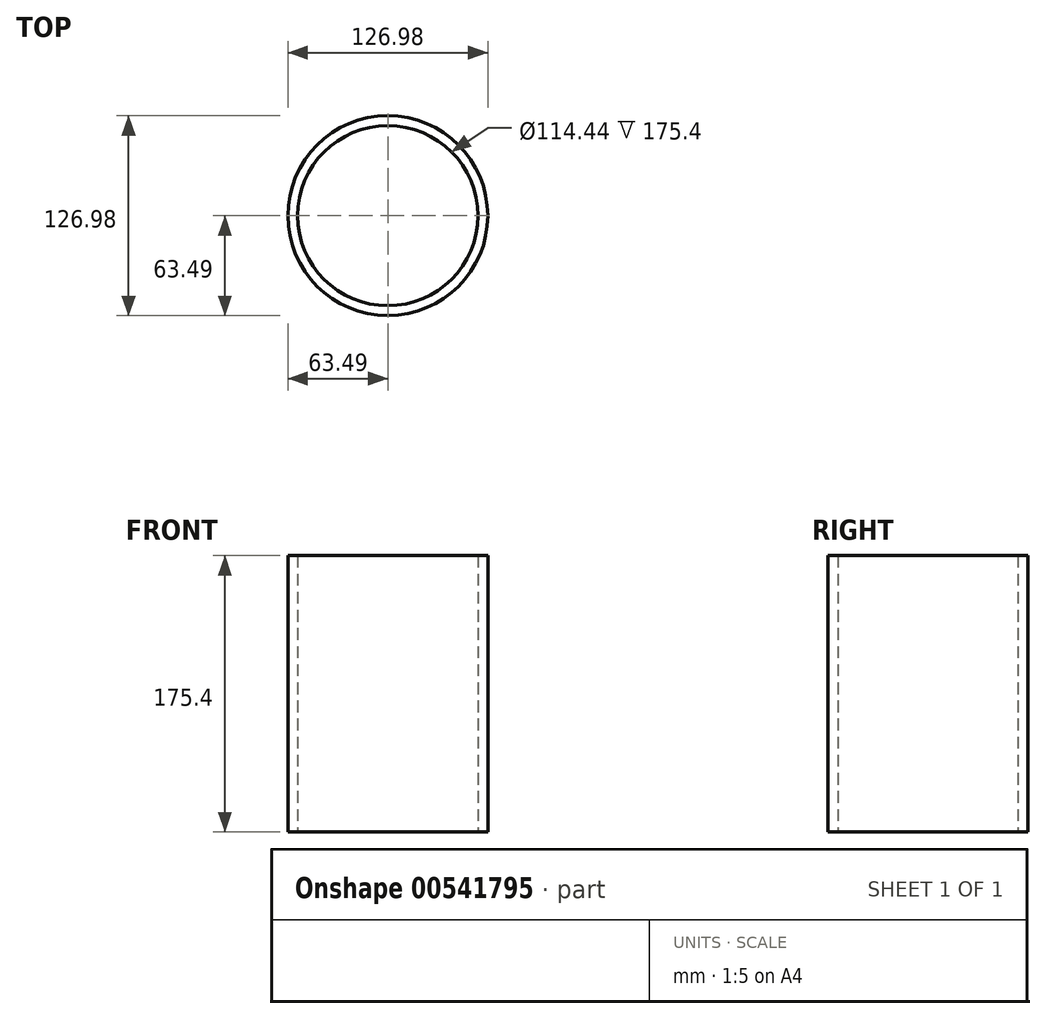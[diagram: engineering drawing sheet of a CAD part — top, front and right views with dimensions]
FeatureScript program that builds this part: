
annotation { "Feature Type Name" : "Feature", "Feature Type Description" : "" }
export const myFeature = defineFeature(function(context is Context, id is Id, definition is map)
    precondition{}
    {
        {
            var Q0;
            Q0=qCreatedBy(makeId("Top.planeOp"),FACE);
            var sketch = newSketch(context, id + "F0", { "sketchPlane" : qUnion([Q0])});
            skCircle(sketch, "E0", {"center": v(0, 0) * mm, "radius": 63.5 * mm});
            skCircle(sketch, "E1", {"center": v(0, 0) * mm, "radius": 57.22 * mm});
            skSolve(sketch);
        }
        {
            var Q0;
            Q0=makeQuery(id+"F0.imprint","IMPRINT",FACE,{"disambiguationData":[TD([[makeQuery(id+"F0.imprint","IMPRINT",EDGE,{"derivedFrom":sQuery(id+"F0.wireOp",EDGE,"E0")}),1.0]])]});
            extrude(context, id + "F1", {"entities" : qUnion([Q0]), "depth" : 150 * mm, "offsetDistance" : 25.4 * mm, "hasSecondDirection" : true, "secondDirectionOppositeDirection" : true, "secondDirectionDepth" : 25.4 * mm});
        }
    });
